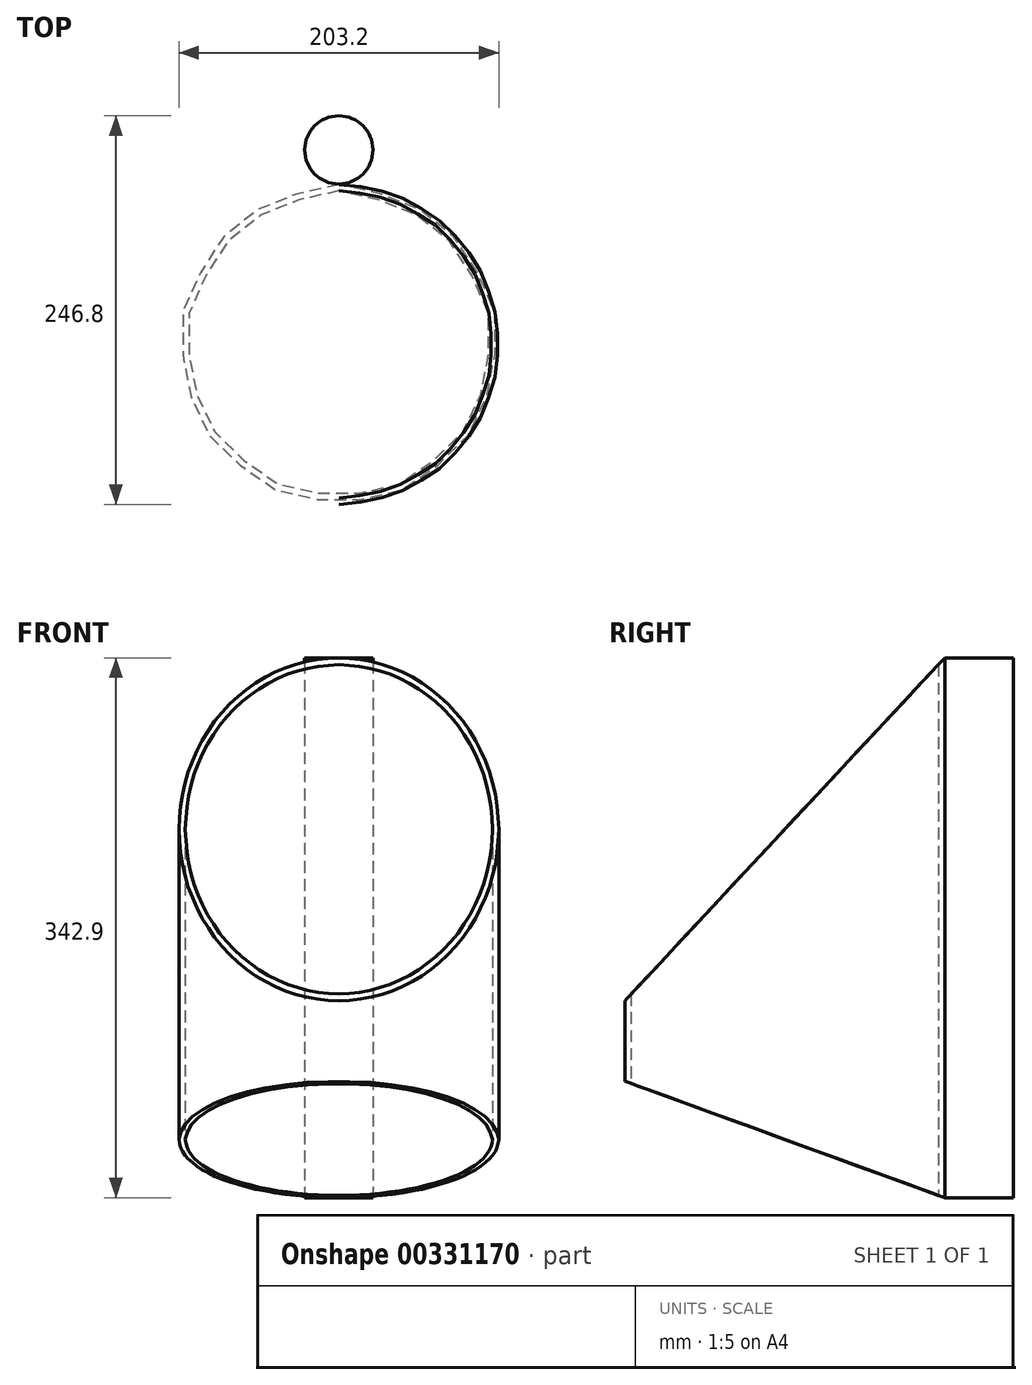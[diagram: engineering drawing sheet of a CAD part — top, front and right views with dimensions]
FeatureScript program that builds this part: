
annotation { "Feature Type Name" : "Feature", "Feature Type Description" : "" }
export const myFeature = defineFeature(function(context is Context, id is Id, definition is map)
    precondition{}
    {
        {
            var Q0;
            Q0=qCreatedBy(makeId("Top.planeOp"),FACE);
            var sketch = newSketch(context, id + "F0", { "sketchPlane" : qUnion([Q0])});
            skCircle(sketch, "E0", {"center": v(0, 0) * mm, "radius": 101.6 * mm});
            skCircle(sketch, "E1.0", {"center": v(0, 0) * mm, "radius": 97.54 * mm});
            skSolve(sketch);
        }
        {
            var Q0;
            Q0 = qSketchRegion(id + "F0", true);
            extrude(context, id + "F1", {"entities" : qUnion([Q0]), "depth" : 342.9 * mm, "offsetDistance" : 25.4 * mm});
        }
        {
            var Q0;
            Q0=qCreatedBy(makeId("Right.planeOp"),FACE);
            var sketch = newSketch(context, id + "F2", { "sketchPlane" : qUnion([Q0])});
            skLineSegment(sketch, "E2.bottom", {"start": v(101.6, 342.9) * mm, "end": v(-101.6, 342.9) * mm});
            skLineSegment(sketch, "E2.right", {"start": v(-101.6, 342.9) * mm, "end": v(-101.6, 125) * mm});
            skPoint(sketch, "E2.middle", {"position": v(0, 233.95) * mm});
            skLineSegment(sketch, "E3.bottom", {"start": v(101.6, 0) * mm, "end": v(-101.6, 0) * mm});
            skLineSegment(sketch, "E3.right", {"start": v(-101.6, 0) * mm, "end": v(-101.6, 73.96) * mm});
            skPoint(sketch, "E3.middle", {"position": v(0, 36.98) * mm});
            skLineSegment(sketch, "E4", {"start": v(-101.6, 125) * mm, "end": v(101.6, 342.9) * mm});
            skPoint(sketch, "E2.top.start.orphan", {"position": v(101.6, 125) * mm});
            skLineSegment(sketch, "E5", {"start": v(-101.6, 73.96) * mm, "end": v(101.6, 0) * mm});
            skPoint(sketch, "E3.left.end.orphan", {"position": v(101.6, 73.96) * mm});
            skLineSegment(sketch, "E6", {"start": v(-101.6, 73.96) * mm, "end": v(101.6, 73.96) * mm});
            skSolve(sketch);
        }
        {
            var Q0;
            Q0 = qSketchRegion(id + "F2", true);
            extrude(context, id + "F3", {"entities" : qUnion([Q0]), "operationType" : NewBodyOperationType.REMOVE, "endBound" : BoundingType.THROUGH_ALL, "depth" : 25.4 * mm, "hasSecondDirection" : true, "secondDirectionBound" : SecondDirectionBoundingType.THROUGH_ALL, "secondDirectionOppositeDirection" : true, "secondDirectionDepth" : 25.4 * mm});
        }
        {
            var Q0;
            Q0=qCreatedBy(makeId("Top.planeOp"),FACE);
            var sketch = newSketch(context, id + "F4", { "sketchPlane" : qUnion([Q0])});
            skCircle(sketch, "E7", {"center": v(0, 123.54) * mm, "radius": 21.66 * mm});
            skSolve(sketch);
        }
        {
            var Q0;
            Q0 = qSketchRegion(id + "F4", true);
            extrude(context, id + "F5", {"entities" : qUnion([Q0]), "depth" : 342.9 * mm, "offsetDistance" : 25.4 * mm});
        }
    });
